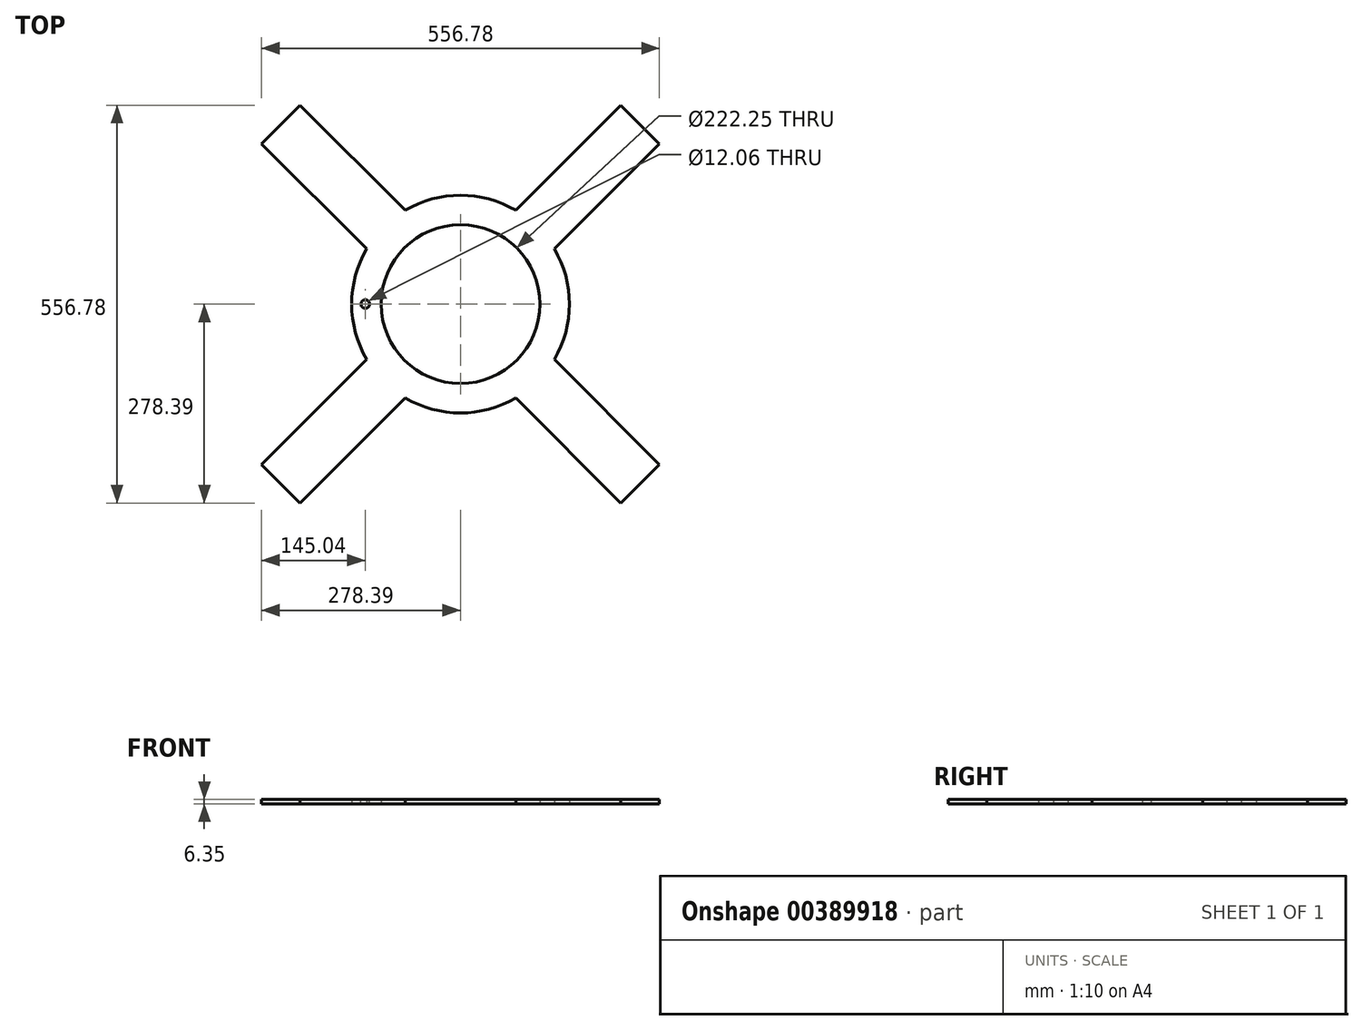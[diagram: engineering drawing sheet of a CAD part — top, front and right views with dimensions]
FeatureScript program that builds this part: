
annotation { "Feature Type Name" : "Feature", "Feature Type Description" : "" }
export const myFeature = defineFeature(function(context is Context, id is Id, definition is map)
    precondition{}
    {
        {
            var Q0;
            Q0=qCreatedBy(makeId("Top.planeOp"),FACE);
            var sketch = newSketch(context, id + "F0", { "sketchPlane" : qUnion([Q0])});
            skArc(sketch, "E0", {"start": v(-131.28, 77.4) * mm, "mid": v(-152.4, 0) * mm, "end": v(-131.28, -77.4) * mm});
            skCircle(sketch, "E1", {"center": v(0, 0) * mm, "radius": 111.13 * mm});
            skLineSegment(sketch, "E2", {"start": v(-278.39, -224.5) * mm, "end": v(-131.28, -77.4) * mm});
            skLineSegment(sketch, "E3", {"start": v(-224.5, -278.39) * mm, "end": v(-77.4, -131.28) * mm});
            skLineSegment(sketch, "E4", {"start": v(224.5, 278.39) * mm, "end": v(278.39, 224.5) * mm});
            skLineSegment(sketch, "E5", {"start": v(-278.39, -224.5) * mm, "end": v(-224.5, -278.39) * mm});
            skLineSegment(sketch, "E6", {"start": v(-278.39, 224.5) * mm, "end": v(-131.28, 77.4) * mm});
            skLineSegment(sketch, "E7", {"start": v(-224.5, 278.39) * mm, "end": v(-77.4, 131.28) * mm});
            skLineSegment(sketch, "E8", {"start": v(-224.5, 278.39) * mm, "end": v(-278.39, 224.5) * mm});
            skLineSegment(sketch, "E9", {"start": v(224.5, -278.39) * mm, "end": v(278.39, -224.5) * mm});
            skArc(sketch, "E10.trimOffspring", {"start": v(77.4, 131.28) * mm, "mid": v(0, 152.4) * mm, "end": v(-77.4, 131.28) * mm});
            skArc(sketch, "E11.trimOffspring", {"start": v(131.28, -77.4) * mm, "mid": v(152.4, 0) * mm, "end": v(131.28, 77.4) * mm});
            skArc(sketch, "E12.trimOffspring", {"start": v(-77.4, -131.28) * mm, "mid": v(0, -152.4) * mm, "end": v(77.4, -131.28) * mm});
            skLineSegment(sketch, "E13.trimOffspring", {"start": v(131.28, 77.4) * mm, "end": v(278.39, 224.5) * mm});
            skLineSegment(sketch, "E14.trimOffspring", {"start": v(77.4, 131.28) * mm, "end": v(224.5, 278.39) * mm});
            skLineSegment(sketch, "E15.trimOffspring", {"start": v(77.4, -131.28) * mm, "end": v(224.5, -278.39) * mm});
            skLineSegment(sketch, "E16.trimOffspring", {"start": v(53.88, 0) * mm, "end": v(100.76, -46.87) * mm});
            skLineSegment(sketch, "E17.trimOffspring", {"start": v(0, -53.88) * mm, "end": v(53.88, 0) * mm});
            skLineSegment(sketch, "E18.trimOffspring", {"start": v(131.28, -77.4) * mm, "end": v(278.39, -224.5) * mm});
            skSolve(sketch);
        }
        {
            var Q0;
            Q0=makeQuery(id+"F0.imprint","IMPRINT",FACE,{"disambiguationData":[TD([[makeQuery(id+"F0.imprint","IMPRINT",EDGE,{"derivedFrom":sQuery(id+"F0.wireOp",EDGE,"E0")}),1.0]])]});
            extrude(context, id + "F1", {"entities" : qUnion([Q0]), "depth" : 6.35 * mm});
        }
        {
            var Q0;
            Q0=makeQuery(id+"F1.opExtrude","CAP_FACE",FACE,{"disambiguationData":[OSD([sQuery(id+"F0.wireOp",EDGE,"E0"),sQuery(id+"F0.wireOp",EDGE,"E1")])],"isStart":false});
            var sketch = newSketch(context, id + "F2", { "sketchPlane" : qUnion([Q0])});
            skCircle(sketch, "E19", {"center": v(-133.35, 0) * mm, "radius": 6.03 * mm});
            skSolve(sketch);
        }
        {
            var Q0;
            Q0=makeQuery(id+"F2.imprint","IMPRINT",FACE,{"disambiguationData":[TD([[makeQuery(id+"F2.imprint","IMPRINT",EDGE,{"derivedFrom":sQuery(id+"F2.wireOp",EDGE,"E19")}),1.0]])]});
            var Q1;
            Q1=sQuery(id+"F2.wireOp",EDGE,"E19");
            extrude(context, id + "F3", {"entities" : qUnion([Q0]), "operationType" : NewBodyOperationType.REMOVE, "surfaceEntities" : qUnion([Q1]), "oppositeDirection" : true, "depth" : 25.4 * mm});
        }
    });
